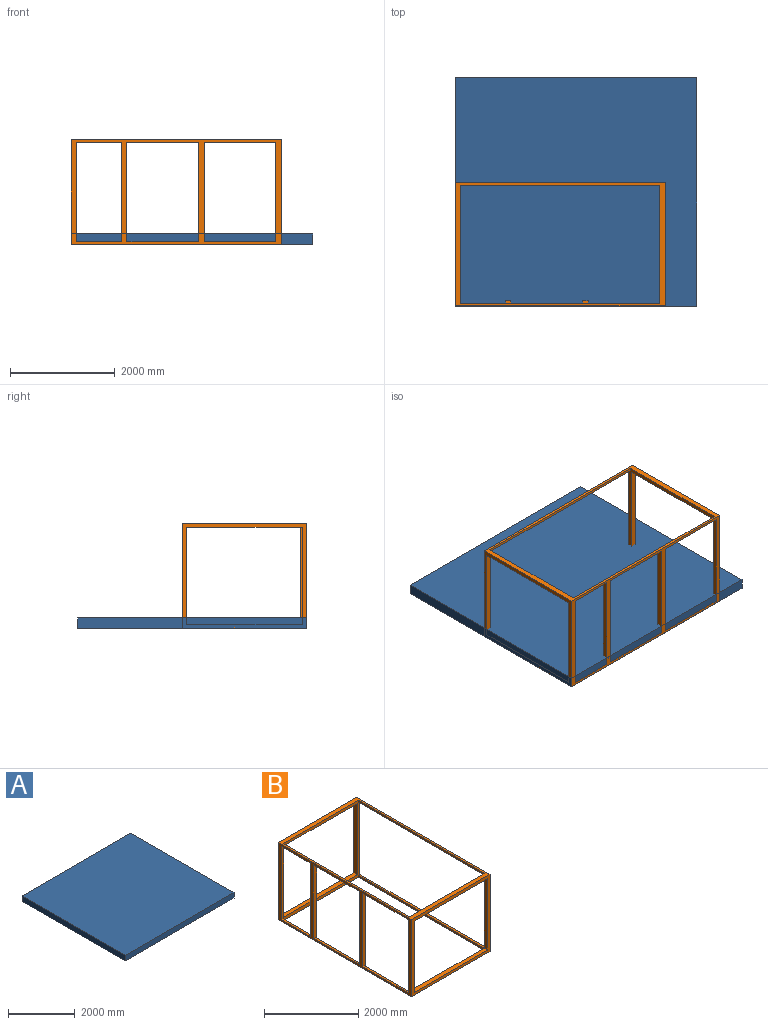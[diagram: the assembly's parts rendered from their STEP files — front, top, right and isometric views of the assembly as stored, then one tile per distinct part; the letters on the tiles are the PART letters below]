
ASSEMBLY  parts=2 mates=1
PART A: 6 faces, bbox 4600x4350x200 mm
  f0: plane 4350x200mm, normal (1,0,0), area 870000mm2, adj f1,f3,f4,f5
  f1: plane 4600x200mm, normal (0,1,0), area 920000mm2, adj f0,f2,f3,f4
  f2: plane 4350x200mm, normal (-1,0,0), area 870000mm2, adj f1,f3,f4,f5
  f3: plane 4600x4350mm, normal (0,0,1), area 20010000mm2, adj f0,f1,f2,f5
  f4: plane 4600x4350mm, normal (0,0,-1), area 20010000mm2, adj f0,f1,f2,f5
  f5: plane 4600x200mm, normal (0,-1,0), area 920000mm2, adj f0,f2,f3,f4
PART B: 38 faces, bbox 2350x4000x2000 mm
  f0: plane 1370x50mm, normal (0,0,-1), area 68500mm2, adj f9,f24,f26,f36
  f1: plane 1370x50mm, normal (0,0,1), area 68500mm2, adj f2,f9,f32,f35
  f2: plane 1370x50mm, normal (1,0,0), area 68500mm2, adj f1,f16,f32,f35
  f3: plane 1370x50mm, normal (0,0,-1), area 68500mm2, adj f9,f26,f32,f35
  f4: plane 860x50mm, normal (0,0,1), area 43000mm2, adj f5,f9,f25,f31
  f5: plane 860x50mm, normal (1,0,0), area 43000mm2, adj f4,f16,f25,f31
  f6: plane 1370x50mm, normal (0,0,1), area 68500mm2, adj f9,f24,f29,f36
  f7: plane 860x50mm, normal (0,0,-1), area 43000mm2, adj f9,f25,f26,f31
  f8: plane 4000x2000mm, normal (1,0,0), area 780000mm2, adj f14,f15,f16,f17,f22,f23,f24,f25
  f9: plane 4000x2000mm, normal (-1,0,0), area 1160000mm2, adj f0,f1,f3,f4,f6,f7,f14,f15
  f10: plane 2200x100mm, normal (0,0,1), area 220000mm2, adj f11,f13,f15,f25
  f11: plane 1850x100mm, normal (-1,0,0), area 185000mm2, adj f10,f12,f15,f25
  f12: plane 2200x100mm, normal (0,0,-1), area 220000mm2, adj f11,f13,f15,f25
  f13: plane 1850x100mm, normal (1,0,0), area 185000mm2, adj f10,f12,f15,f25
  f14: plane 2350x2000mm, normal (0,-1,0), area 630000mm2, adj f8,f9,f16,f17,f18,f19,f20,f21
  f15: plane 2350x2000mm, normal (0,1,0), area 630000mm2, adj f8,f9,f10,f11,f12,f13,f16,f17
  f16: plane 4000x2350mm, normal (0,0,-1), area 860000mm2, adj f2,f5,f8,f9,f14,f15,f24,f25
  f17: plane 4000x2350mm, normal (0,0,1), area 850000mm2, adj f8,f9,f14,f15,f24,f25,f26,f27
  f18: plane 2200x100mm, normal (0,0,1), area 220000mm2, adj f14,f19,f21,f24
  f19: plane 1850x100mm, normal (-1,0,0), area 185000mm2, adj f14,f18,f20,f24
  f20: plane 2200x100mm, normal (0,0,-1), area 220000mm2, adj f14,f19,f21,f24
  f21: plane 1850x100mm, normal (1,0,0), area 185000mm2, adj f14,f18,f20,f24
  f22: plane 3800x50mm, normal (0,0,1), area 190000mm2, adj f8,f24,f25,f28
  f23: plane 3800x50mm, normal (0,0,-1), area 190000mm2, adj f8,f24,f25,f27
  f24: plane 2350x2000mm, normal (0,1,0), area 620000mm2, adj f0,f6,f8,f9,f16,f17,f18,f19
  f25: plane 2350x2000mm, normal (0,-1,0), area 620000mm2, adj f4,f5,f7,f8,f9,f10,f11,f12
  f26: plane 3800x50mm, normal (1,0,0), area 190000mm2, adj f0,f3,f7,f17,f24,f25,f30,f34
  f27: plane 3800x50mm, normal (-1,0,0), area 190000mm2, adj f17,f23,f24,f25
  f28: plane 3800x50mm, normal (-1,0,0), area 190000mm2, adj f16,f22,f24,f25
  f29: plane 1370x50mm, normal (1,0,0), area 68500mm2, adj f6,f16,f24,f36
  f30: plane 100x50mm, normal (0,0,1), area 5000mm2, adj f26,f31,f32,f33
  f31: plane 1950x100mm, normal (0,1,0), area 192500mm2, adj f4,f5,f7,f9,f16,f30,f33
  f32: plane 1950x100mm, normal (0,-1,0), area 192500mm2, adj f1,f2,f3,f9,f16,f30,f33
  f33: plane 1950x100mm, normal (1,0,0), area 195000mm2, adj f16,f30,f31,f32
  f34: plane 100x50mm, normal (0,0,1), area 5000mm2, adj f26,f35,f36,f37
  f35: plane 1950x100mm, normal (0,1,0), area 192500mm2, adj f1,f2,f3,f9,f16,f34,f37
  f36: plane 1950x100mm, normal (0,-1,0), area 192500mm2, adj f0,f6,f9,f16,f29,f34,f37
  f37: plane 1950x100mm, normal (1,0,0), area 195000mm2, adj f16,f34,f35,f36
PLACE A t=(0,205,0)mm
PLACE B rot(axis=(0,0,1),90deg) t=(-2300,-1000,1000)mm
MATE fastened B.f16 <-> A.f4  axis (0,0,-1) through (-2300,-2175,0)mm
